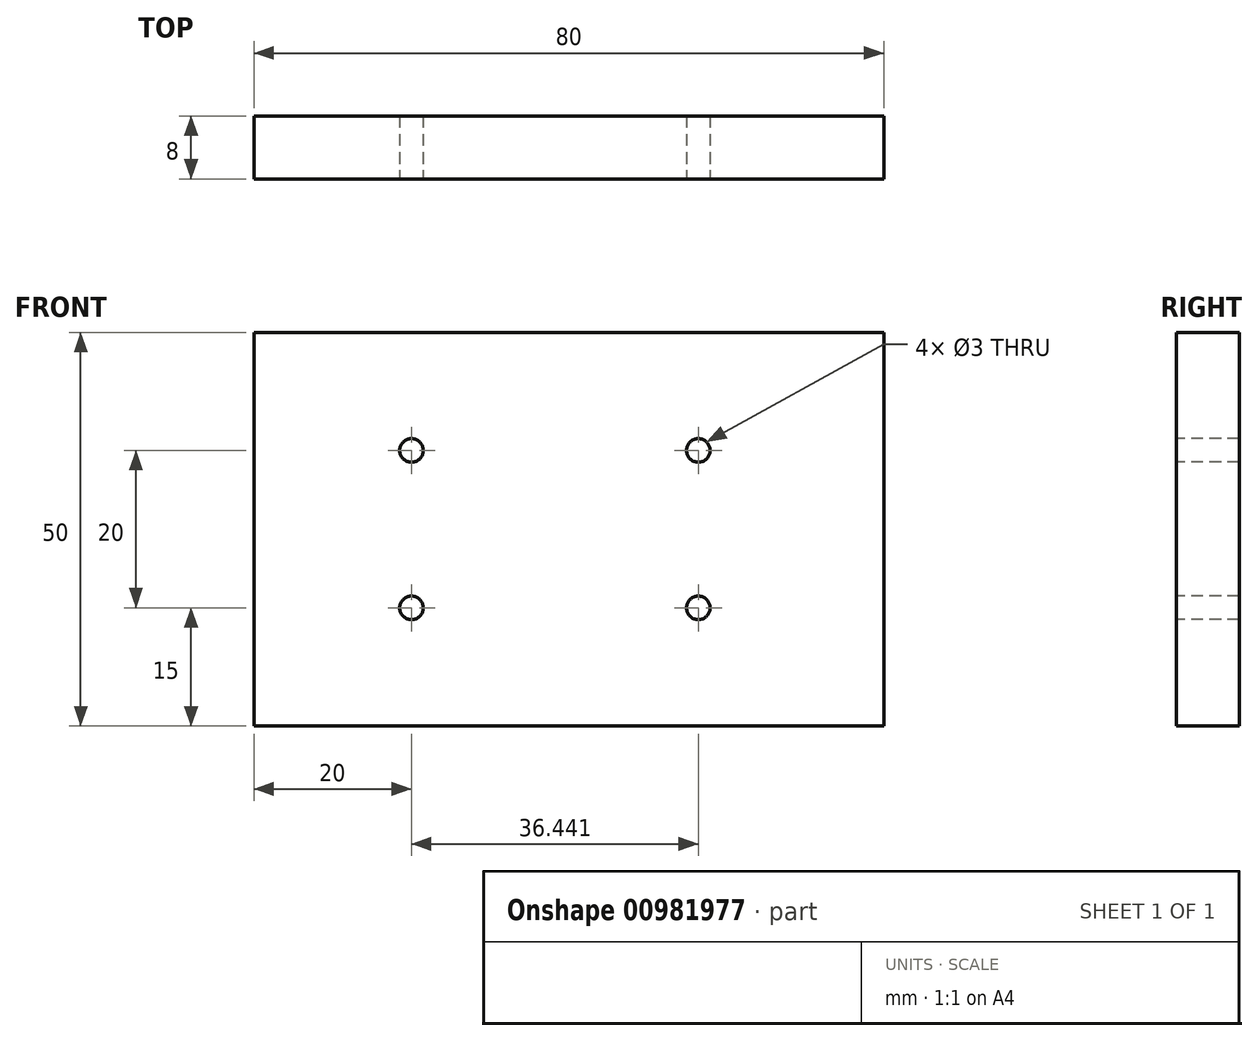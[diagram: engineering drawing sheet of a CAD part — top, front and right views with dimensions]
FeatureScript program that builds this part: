
annotation { "Feature Type Name" : "Feature", "Feature Type Description" : "" }
export const myFeature = defineFeature(function(context is Context, id is Id, definition is map)
    precondition{}
    {
        {
            var Q0;
            Q0=qCreatedBy(makeId("Front.planeOp"),FACE);
            var sketch = newSketch(context, id + "F0", { "sketchPlane" : qUnion([Q0])});
            skLineSegment(sketch, "E0.bottom", {"start": v(41.78, 25) * mm, "end": v(-38.22, 25) * mm});
            skLineSegment(sketch, "E0.top", {"start": v(41.78, -25) * mm, "end": v(-38.22, -25) * mm});
            skLineSegment(sketch, "E0.left", {"start": v(41.78, 25) * mm, "end": v(41.78, -25) * mm});
            skLineSegment(sketch, "E0.right", {"start": v(-38.22, 25) * mm, "end": v(-38.22, -25) * mm});
            skPoint(sketch, "E0.middle", {"position": v(1.78, 0) * mm});
            skSolve(sketch);
        }
        {
            var Q0;
            Q0 = qSketchRegion(id + "F0", true);
            extrude(context, id + "F1", {"entities" : qUnion([Q0]), "depth" : 8 * mm, "offsetDistance" : 25 * mm});
        }
        {
            var Q0;
            Q0=makeQuery(id+"F1.opExtrude","CAP_FACE",FACE,{"disambiguationData":[OSD([sQuery(id+"F0.wireOp",EDGE,"E0.bottom"),sQuery(id+"F0.wireOp",EDGE,"E0.top"),sQuery(id+"F0.wireOp",EDGE,"E0.left"),sQuery(id+"F0.wireOp",EDGE,"E0.right")])],"isStart":false});
            var sketch = newSketch(context, id + "F2", { "sketchPlane" : qUnion([Q0])});
            skCircle(sketch, "E1", {"center": v(-18.22, 10) * mm, "radius": 1.5 * mm});
            skCircle(sketch, "E2", {"center": v(-18.22, -10) * mm, "radius": 1.5 * mm});
            skCircle(sketch, "E3.MirrorC", {"center": v(18.22, -10) * mm, "radius": 1.5 * mm});
            skCircle(sketch, "E4.MirrorC", {"center": v(18.22, 10) * mm, "radius": 1.5 * mm});
            skSolve(sketch);
        }
        {
            var Q0;
            Q0 = qSketchRegion(id + "F2", true);
            extrude(context, id + "F3", {"entities" : qUnion([Q0]), "operationType" : NewBodyOperationType.REMOVE, "oppositeDirection" : true, "depth" : 25 * mm, "offsetDistance" : 25 * mm});
        }
    });
